# Revit family: ledpanels-e4_sq620-32w-840-u19_542003098800
name_source: partatom
category: Leuchten
revit_build: Autodesk Revit 2016 (Build: 20190508_0715(x64)
units: mm (PartAtom-declared; Revit-internal decimal feet)

## family parameters
Basisbauteil = Fläche
Beim Laden mit Abzugskörper schneiden = Nein
Bemaßung runder Anschluss = Durchmesser verwenden
Gemeinsam genutzt = Nein
Lichtquelle = Nein
Raumberechnungspunkt = Nein
Teiletyp = Normal

## types (1)
- LEDPanelS-E4 Sq620-32W-840-U19 (1 x LED, 4100 lm, 4000)
    Approval mark = CE, ENEC
    Beschreibung = LED Slim Panel, suitable for offices (UGR19). Suitable for recessed and suspended applications. Recessed ceiling frame and surface module kit available as accessory.
    CIE Flux Codes = 59 86 97 100 100
    Color Rendering = 80
    Color Temperature = 4000
    Control Gear = Electronic ballast
    Frequency = 60 Hz
    Height = 35 mm
    Hersteller = OPPLE
    Lamp Light Flux = 4100 lm
    Lamp count = 1
    Lampe = 1 x LED
    Length = 620 mm
    Luminous efficacy = 128 lm/W
    ModVariant = Nein
    Modell = 542003098800
    Mounting Place = Ceiling
    Mounting Type = Recessed, Surface mounted
    Number of Poles = 1
    OnlyDefault = Ja
    Power Factor = 1
    Product Name = LEDPanelS-E4 Sq620-32W-840-U19
    Product group = Ceiling mounted luminaire
    ProductGroupID = 3
    Protection Class = Protection class II
    Protection Degree = IP 20
    RLX_Detail_Level = 1
    RlxData = <blob elided: 128117 chars, md5=3fd44485>
    Scheinlast = 32 VA
    Socket = socket
    Standby Power = 0 W
    System Light Flux = 4100 lm
    System Power = 32 W
    Typenbild = slimp_e4_v2.jpg
    Typenkommentare = Product without accessories
    URL = http://relux.com
    VarID = ---
    Voltage = 230 V
    Voltage Range = 220-240 V
    Vorgabe-Ansicht = 1800 mm
    Weight = 0.00 kg
    Width = 620 mm

## geometry (parser evidence)
native form markers: Blend x4, Sweep x11
no freeform markers — native parametric forms only
